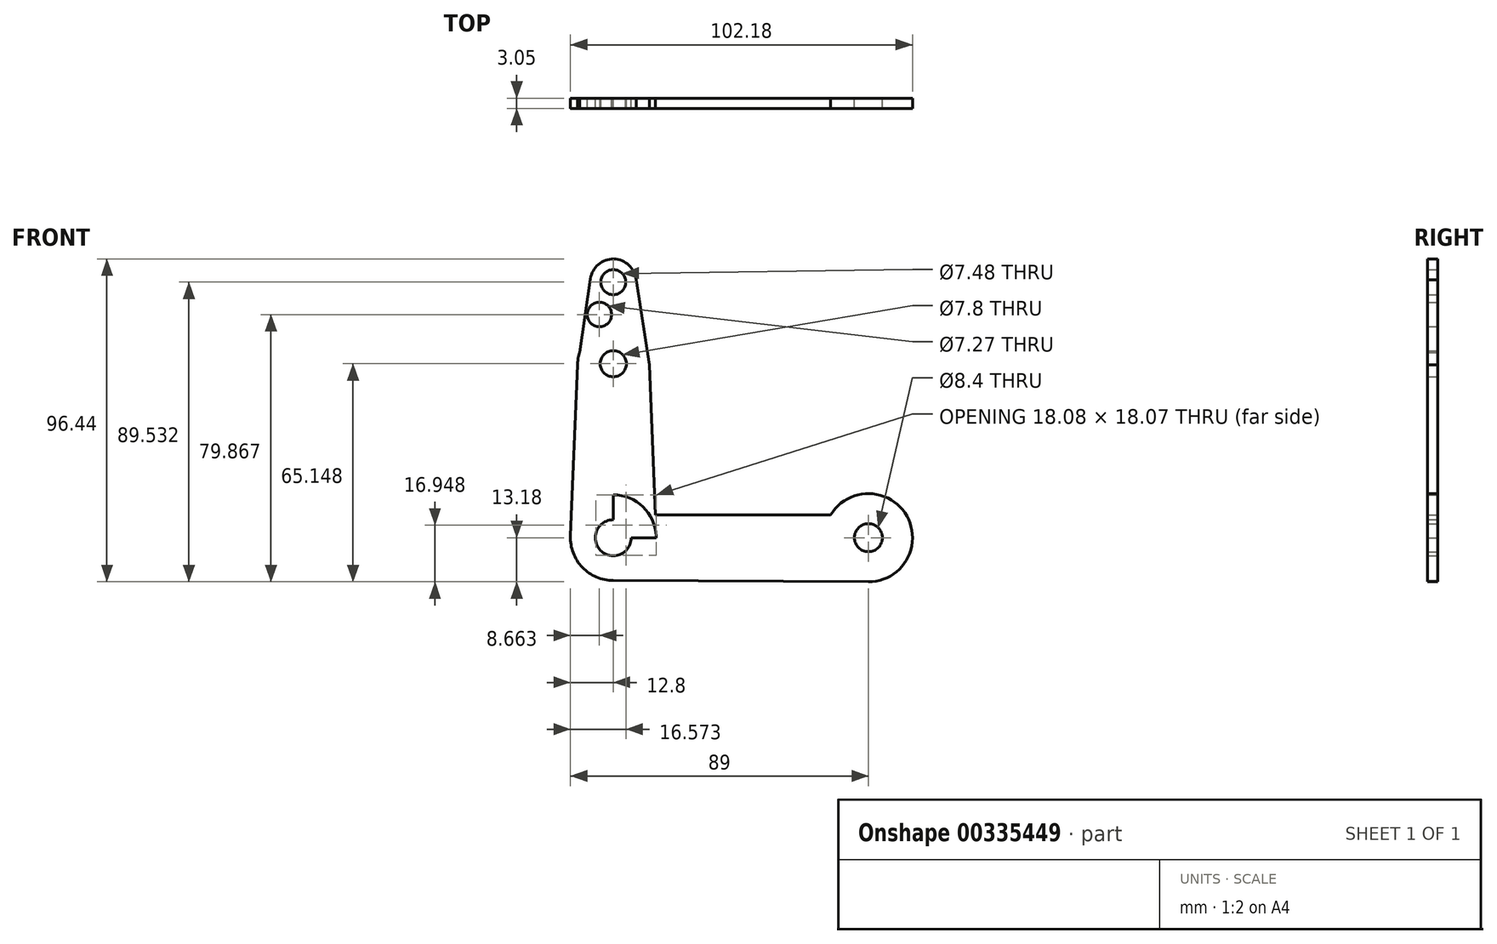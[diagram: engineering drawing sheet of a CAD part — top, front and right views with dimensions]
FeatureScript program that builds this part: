
annotation { "Feature Type Name" : "Feature", "Feature Type Description" : "" }
export const myFeature = defineFeature(function(context is Context, id is Id, definition is map)
    precondition{}
    {
        {
            var Q0;
            Q0=qCreatedBy(makeId("Front.planeOp"),FACE);
            var sketch = newSketch(context, id + "F0", { "sketchPlane" : qUnion([Q0])});
            skLineSegment(sketch, "E0", {"start": v(0, 76.35) * mm, "end": v(0, 0) * mm});
            skCircle(sketch, "E1", {"center": v(0, 76.35) * mm, "radius": 6.91 * mm});
            skCircle(sketch, "E2", {"center": v(0, 51.97) * mm, "radius": 10.63 * mm});
            skCircle(sketch, "E3", {"center": v(0, 0) * mm, "radius": 12.8 * mm});
            skCircle(sketch, "E4", {"center": v(76.2, 0) * mm, "radius": 13.18 * mm});
            skLineSegment(sketch, "E5", {"start": v(0, 0) * mm, "end": v(0, 51.97) * mm});
            skLineSegment(sketch, "E6", {"start": v(0, 0) * mm, "end": v(76.2, 0) * mm});
            skLineSegment(sketch, "E7", {"start": v(-6.84, 77.36) * mm, "end": v(-10.63, 51.62) * mm});
            skLineSegment(sketch, "E8", {"start": v(6.76, 77.78) * mm, "end": v(10.81, 51.62) * mm});
            skLineSegment(sketch, "E9", {"start": v(-10.63, 51.62) * mm, "end": v(-12.81, 0) * mm});
            skLineSegment(sketch, "E10", {"start": v(10.81, 51.62) * mm, "end": v(12.81, 0) * mm});
            skLineSegment(sketch, "E11", {"start": v(10.81, 6.85) * mm, "end": v(64.94, 6.85) * mm});
            skLineSegment(sketch, "E12", {"start": v(0, -12.8) * mm, "end": v(76.14, -13.18) * mm});
            skCircle(sketch, "E13", {"center": v(0, 76.35) * mm, "radius": 3.74 * mm});
            skCircle(sketch, "E14", {"center": v(0, 51.97) * mm, "radius": 3.9 * mm});
            skCircle(sketch, "E15", {"center": v(0, 0) * mm, "radius": 5.37 * mm});
            skCircle(sketch, "E16", {"center": v(76.2, 0) * mm, "radius": 4.2 * mm});
            skCircle(sketch, "E17", {"center": v(-4.14, 66.69) * mm, "radius": 3.64 * mm});
            skSolve(sketch);
        }
        {
            var Q0;
            Q0 = qSketchRegion(id + "F0", true);
            extrude(context, id + "F1", {"entities" : qUnion([Q0]), "depth" : 3.05 * mm});
        }
    });
